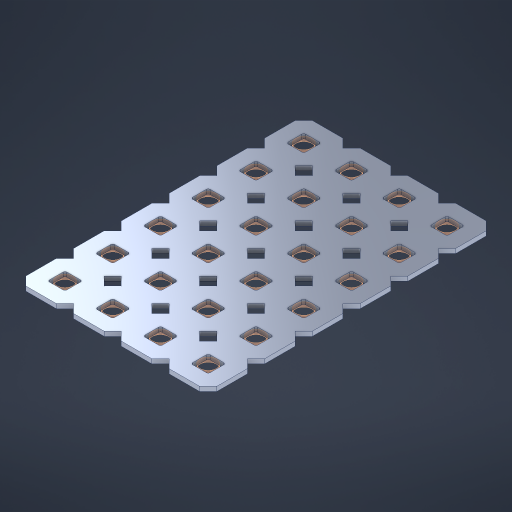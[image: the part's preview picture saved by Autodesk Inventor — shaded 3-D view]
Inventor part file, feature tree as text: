
AUTODESK INVENTOR PART (.ipt)
format: ipt  version: 2023 (Build 270158000, 158)  size: 539,136 bytes
history: native  units: in
note: dims shown in document units (in); Inventor stores cm internally (conversion verified against a paired STEP export)
features: other x25, extrude x23, sketch x2, pattern_linear x1
ambient origin geometry x8: Origin, YZ Plane, XZ Plane, XY Plane, X Axis, Y Axis, Z Axis, Center Point
bodies: Solid1 (feature_tree), Body (feature_tree)
feature tree (51):
  pattern_linear  "Rectangular Pattern1"  Spacing1=0.09in  [1 undecoded]
  sketch  "Sketch1"  dims[d1=0.5in]
  sketch  "Sketch2"  dims[d2=0.182in d3=0.09in d4=0.09in d5=0.09in d6=0.09in d7=0.09in d8=0.09in d9=0.09in d10=0.09in d11=0.02in d13=0.0in d14=0.172in d15=0.0625in d16=0.0in d19=0.5in d22=0.5in]
  other  "Srf1"
  other  "Srf126"
  other  "Srf127"
  other  "Srf128"
  other  "Srf129"
  other  "Srf130"
  other  "Srf268"
  other  "Srf269"
  other  "Srf270"
  other  "Srf271"
  other  "Srf272"
  other  "Srf273"
  other  "Srf293"
  other  "Srf294"
  other  "Srf295"
  other  "Srf296"
  other  "Srf297"
  other  "Srf298"
  other  "Srf318"
  other  "Srf319"
  other  "Srf320"
  other  "Srf321"
  other  "Srf322"
  other  "Srf323"
  other  "Circle"
  extrude  "ExtrusionSrf126"  Depth=0.09in
  extrude  "ExtrusionSrf127"  Depth=0.09in
  extrude  "ExtrusionSrf128"  Depth=0.09in
  extrude  "ExtrusionSrf129"  Depth=0.09in
  extrude  "ExtrusionSrf130"  Depth=0.09in
  extrude  "ExtrusionSrf268"  Depth=0.09in
  extrude  "ExtrusionSrf269"  Depth=0.09in
  extrude  "ExtrusionSrf270"  Depth=0.02in
  extrude  "ExtrusionSrf271"  TaperAngle=0.0deg  [1 undecoded]
  extrude  "ExtrusionSrf272"  Depth=0.5in
  extrude  "ExtrusionSrf273"  Depth=0.5in TaperAngle=0.0deg
  extrude  "ExtrusionSrf293"  Depth=0.5in
  extrude  "ExtrusionSrf294"  Depth=0.5in
  extrude  "ExtrusionSrf295"  [1 undecoded]
  extrude  "ExtrusionSrf296"  [1 undecoded]
  extrude  "ExtrusionSrf297"  [1 undecoded]
  extrude  "ExtrusionSrf298"  [1 undecoded]
  extrude  "ExtrusionSrf318"  [1 undecoded]
  extrude  "ExtrusionSrf319"  [1 undecoded]
  extrude  "ExtrusionSrf320"  [1 undecoded]
  extrude  "ExtrusionSrf321"  [1 undecoded]
  extrude  "ExtrusionSrf322"  [1 undecoded]
  extrude  "ExtrusionSrf323"  [1 undecoded]
note: 12 required parameter values undecoded (feature->parameter linkage not recoverable at this tier; creation-order binding heuristic only, values carry confidence <= 0.55)
